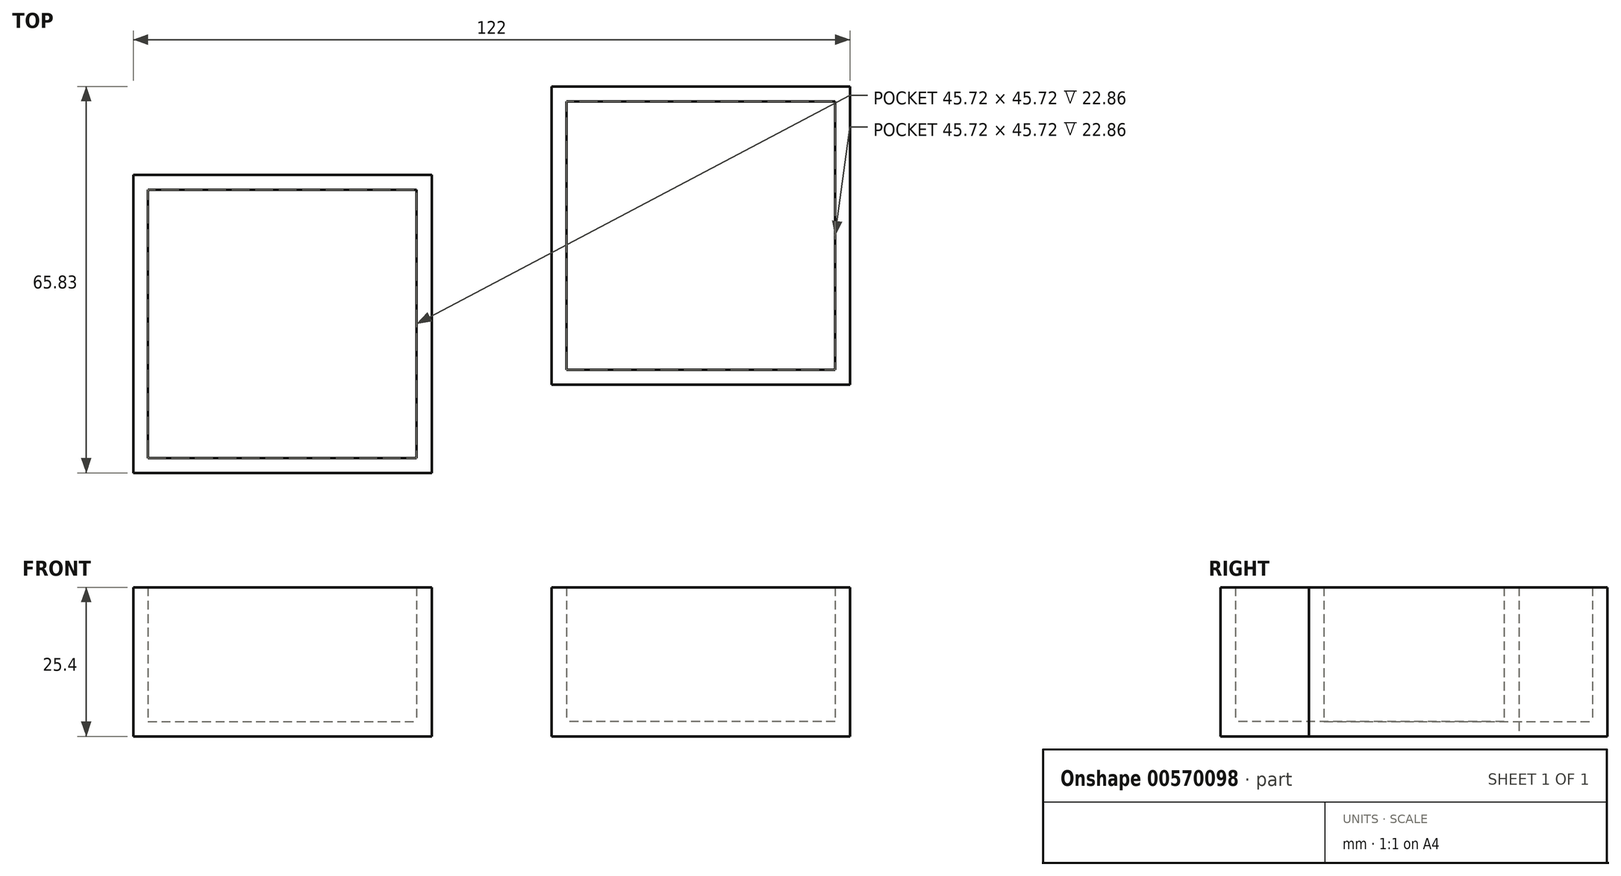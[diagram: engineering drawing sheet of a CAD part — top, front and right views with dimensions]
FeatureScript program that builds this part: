
annotation { "Feature Type Name" : "Feature", "Feature Type Description" : "" }
export const myFeature = defineFeature(function(context is Context, id is Id, definition is map)
    precondition{}
    {
        {
            var Q0;
            Q0=qCreatedBy(makeId("Top.planeOp"),FACE);
            var sketch = newSketch(context, id + "F0", { "sketchPlane" : qUnion([Q0])});
            skLineSegment(sketch, "E0.bottom", {"start": v(-67.7, 71.36) * mm, "end": v(-16.9, 71.36) * mm});
            skLineSegment(sketch, "E0.top", {"start": v(-67.7, 20.56) * mm, "end": v(-16.9, 20.56) * mm});
            skLineSegment(sketch, "E0.left", {"start": v(-67.7, 71.36) * mm, "end": v(-67.7, 20.56) * mm});
            skLineSegment(sketch, "E0.right", {"start": v(-16.9, 71.36) * mm, "end": v(-16.9, 20.56) * mm});
            skSolve(sketch);
        }
        {
            var Q0;
            Q0=qCreatedBy(makeId("Top.planeOp"),FACE);
            var sketch = newSketch(context, id + "F1", { "sketchPlane" : qUnion([Q0])});
            skLineSegment(sketch, "E1.bottom", {"start": v(54.31, 35.6) * mm, "end": v(3.51, 35.6) * mm});
            skLineSegment(sketch, "E1.top", {"start": v(54.31, 86.4) * mm, "end": v(3.51, 86.4) * mm});
            skLineSegment(sketch, "E1.left", {"start": v(54.31, 35.6) * mm, "end": v(54.31, 86.4) * mm});
            skLineSegment(sketch, "E1.right", {"start": v(3.51, 35.6) * mm, "end": v(3.51, 86.4) * mm});
            skSolve(sketch);
        }
        {
            var Q0;
            Q0=makeQuery(id+"F0.imprint","IMPRINT",FACE,{"disambiguationData":[TD([[makeQuery(id+"F0.imprint","IMPRINT",EDGE,{"derivedFrom":sQuery(id+"F0.wireOp",EDGE,"E0.bottom")}),-1.0]])]});
            extrude(context, id + "F2", {"entities" : qUnion([Q0]), "depth" : 25.4 * mm, "offsetDistance" : 25.4 * mm});
        }
        {
            var Q0;
            Q0=makeQuery(id+"F1.imprint","IMPRINT",FACE,{"disambiguationData":[TD([[makeQuery(id+"F1.imprint","IMPRINT",EDGE,{"derivedFrom":sQuery(id+"F1.wireOp",EDGE,"E1.bottom")}),-1.0]])]});
            extrude(context, id + "F3", {"entities" : qUnion([Q0]), "depth" : 25.4 * mm, "offsetDistance" : 25.4 * mm});
        }
        {
            var Q0;
            Q0=makeQuery(id+"F3.opExtrude","CAP_FACE",FACE,{"disambiguationData":[OSD([sQuery(id+"F1.wireOp",EDGE,"E1.bottom"),sQuery(id+"F1.wireOp",EDGE,"E1.top"),sQuery(id+"F1.wireOp",EDGE,"E1.left"),sQuery(id+"F1.wireOp",EDGE,"E1.right")])],"isStart":false});
            var Q1;
            Q1=makeQuery(id+"F2.opExtrude","CAP_FACE",FACE,{"disambiguationData":[OSD([sQuery(id+"F0.wireOp",EDGE,"E0.bottom"),sQuery(id+"F0.wireOp",EDGE,"E0.top"),sQuery(id+"F0.wireOp",EDGE,"E0.left"),sQuery(id+"F0.wireOp",EDGE,"E0.right")])],"isStart":false});
            shell(context, id + "F4", {"entities" : qUnion([Q0, Q1]), "thickness" : 2.54 * mm});
        }
    });
